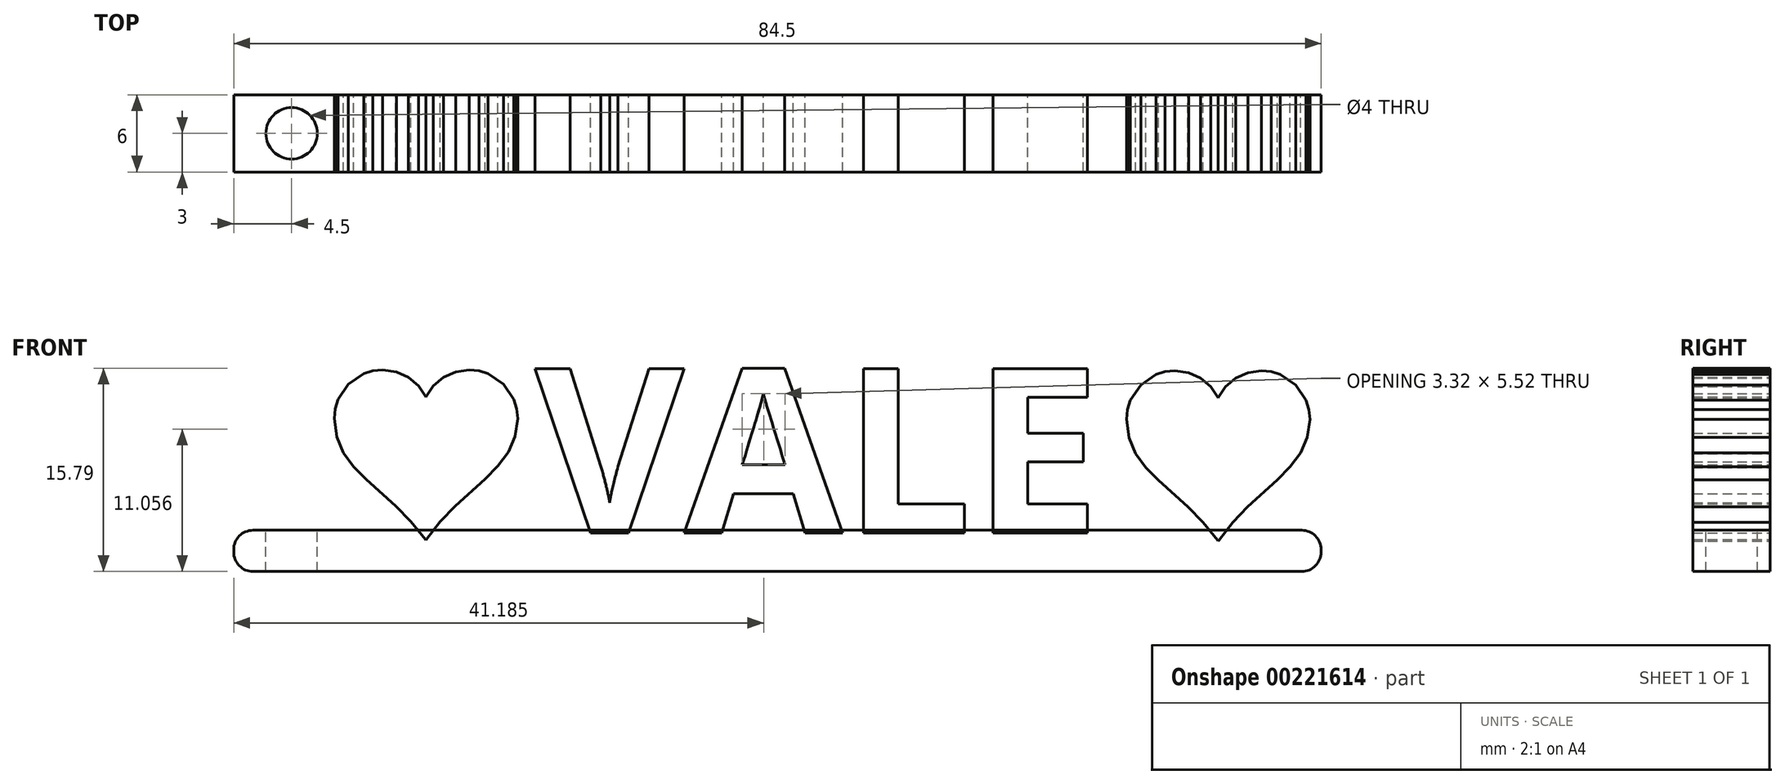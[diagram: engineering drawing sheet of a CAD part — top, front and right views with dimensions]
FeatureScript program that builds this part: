
annotation { "Feature Type Name" : "Feature", "Feature Type Description" : "" }
export const myFeature = defineFeature(function(context is Context, id is Id, definition is map)
    precondition{}
    {
        {
            var Q0;
            Q0=qCreatedBy(makeId("Front.planeOp"),FACE);
            var sketch = newSketch(context, id + "F0", { "sketchPlane" : qUnion([Q0])});
            skText(sketch, "E0", { "text": "   VALE", "fontName": "OpenSans-Bold.ttf"});
            skLineSegment(sketch, "E1", {"start": v(45.25, 12.6) * mm, "end": v(44.49, 12.52) * mm});
            skLineSegment(sketch, "E2", {"start": v(44.49, 12.52) * mm, "end": v(43.78, 12.3) * mm});
            skLineSegment(sketch, "E3", {"start": v(43.78, 12.3) * mm, "end": v(42.58, 11.5) * mm});
            skLineSegment(sketch, "E4", {"start": v(42.58, 11.5) * mm, "end": v(41.78, 10.3) * mm});
            skLineSegment(sketch, "E5", {"start": v(41.78, 10.3) * mm, "end": v(41.56, 9.59) * mm});
            skLineSegment(sketch, "E6", {"start": v(41.56, 9.59) * mm, "end": v(41.48, 8.83) * mm});
            skLineSegment(sketch, "E7", {"start": v(41.48, 8.83) * mm, "end": v(41.67, 7.39) * mm});
            skLineSegment(sketch, "E8", {"start": v(41.67, 7.39) * mm, "end": v(42.19, 6.16) * mm});
            skLineSegment(sketch, "E9", {"start": v(42.19, 6.16) * mm, "end": v(42.98, 5.08) * mm});
            skLineSegment(sketch, "E10", {"start": v(42.98, 5.08) * mm, "end": v(43.96, 4.08) * mm});
            skLineSegment(sketch, "E11", {"start": v(43.96, 4.08) * mm, "end": v(46.26, 2.03) * mm});
            skLineSegment(sketch, "E12", {"start": v(46.26, 2.03) * mm, "end": v(47.44, 0.82) * mm});
            skLineSegment(sketch, "E13", {"start": v(47.44, 0.82) * mm, "end": v(48.56, -0.59) * mm});
            skLineSegment(sketch, "E14", {"start": v(48.56, -0.59) * mm, "end": v(48.6, -0.65) * mm});
            skLineSegment(sketch, "E15", {"start": v(48.6, -0.65) * mm, "end": v(48.65, -0.59) * mm});
            skLineSegment(sketch, "E16", {"start": v(48.65, -0.59) * mm, "end": v(49.73, 0.82) * mm});
            skLineSegment(sketch, "E17", {"start": v(49.73, 0.82) * mm, "end": v(50.9, 2.03) * mm});
            skLineSegment(sketch, "E18", {"start": v(50.9, 2.03) * mm, "end": v(53.2, 4.12) * mm});
            skLineSegment(sketch, "E19", {"start": v(53.2, 4.12) * mm, "end": v(54.2, 5.13) * mm});
            skLineSegment(sketch, "E20", {"start": v(54.2, 5.13) * mm, "end": v(55, 6.21) * mm});
            skLineSegment(sketch, "E21", {"start": v(55, 6.21) * mm, "end": v(55.54, 7.42) * mm});
            skLineSegment(sketch, "E22", {"start": v(55.54, 7.42) * mm, "end": v(55.73, 8.83) * mm});
            skLineSegment(sketch, "E23", {"start": v(55.73, 8.83) * mm, "end": v(55.66, 9.59) * mm});
            skLineSegment(sketch, "E24", {"start": v(55.66, 9.59) * mm, "end": v(55.44, 10.3) * mm});
            skLineSegment(sketch, "E25", {"start": v(55.44, 10.3) * mm, "end": v(54.63, 11.5) * mm});
            skLineSegment(sketch, "E26", {"start": v(54.63, 11.5) * mm, "end": v(53.43, 12.3) * mm});
            skLineSegment(sketch, "E27", {"start": v(53.43, 12.3) * mm, "end": v(52.72, 12.52) * mm});
            skLineSegment(sketch, "E28", {"start": v(52.72, 12.52) * mm, "end": v(51.97, 12.6) * mm});
            skLineSegment(sketch, "E29", {"start": v(51.97, 12.6) * mm, "end": v(50.9, 12.44) * mm});
            skLineSegment(sketch, "E30", {"start": v(50.9, 12.44) * mm, "end": v(49.96, 12.01) * mm});
            skLineSegment(sketch, "E31", {"start": v(49.96, 12.01) * mm, "end": v(49.18, 11.35) * mm});
            skLineSegment(sketch, "E32", {"start": v(49.18, 11.35) * mm, "end": v(48.6, 10.5) * mm});
            skLineSegment(sketch, "E33", {"start": v(48.6, 10.5) * mm, "end": v(48.03, 11.35) * mm});
            skLineSegment(sketch, "E34", {"start": v(48.03, 11.35) * mm, "end": v(47.25, 12.01) * mm});
            skLineSegment(sketch, "E35", {"start": v(47.25, 12.01) * mm, "end": v(46.3, 12.44) * mm});
            skLineSegment(sketch, "E36", {"start": v(46.3, 12.44) * mm, "end": v(45.25, 12.6) * mm});
            skLineSegment(sketch, "E37", {"start": v(39.6, 12.85) * mm, "end": v(71.85, 12.85) * mm, "construction": true});
            skLineSegment(sketch, "E38", {"start": v(-16.32, 12.66) * mm, "end": v(-17.08, 12.59) * mm});
            skLineSegment(sketch, "E39", {"start": v(-17.08, 12.59) * mm, "end": v(-17.78, 12.37) * mm});
            skLineSegment(sketch, "E40", {"start": v(-17.78, 12.37) * mm, "end": v(-18.98, 11.56) * mm});
            skLineSegment(sketch, "E41", {"start": v(-18.98, 11.56) * mm, "end": v(-19.79, 10.36) * mm});
            skLineSegment(sketch, "E42", {"start": v(-19.79, 10.36) * mm, "end": v(-20, 9.65) * mm});
            skLineSegment(sketch, "E43", {"start": v(-20, 9.65) * mm, "end": v(-20.09, 8.9) * mm});
            skLineSegment(sketch, "E44", {"start": v(-20.09, 8.9) * mm, "end": v(-19.9, 7.45) * mm});
            skLineSegment(sketch, "E45", {"start": v(-19.9, 7.45) * mm, "end": v(-19.38, 6.22) * mm});
            skLineSegment(sketch, "E46", {"start": v(-19.38, 6.22) * mm, "end": v(-18.6, 5.15) * mm});
            skLineSegment(sketch, "E47", {"start": v(-18.6, 5.15) * mm, "end": v(-17.6, 4.15) * mm});
            skLineSegment(sketch, "E48", {"start": v(-17.6, 4.15) * mm, "end": v(-15.31, 2.09) * mm});
            skLineSegment(sketch, "E49", {"start": v(-15.31, 2.09) * mm, "end": v(-14.13, 0.89) * mm});
            skLineSegment(sketch, "E50", {"start": v(-14.13, 0.89) * mm, "end": v(-13, -0.52) * mm});
            skLineSegment(sketch, "E51", {"start": v(-13, -0.52) * mm, "end": v(-12.96, -0.59) * mm});
            skLineSegment(sketch, "E52", {"start": v(-12.96, -0.59) * mm, "end": v(-12.92, -0.52) * mm});
            skLineSegment(sketch, "E53", {"start": v(-12.92, -0.52) * mm, "end": v(-11.84, 0.89) * mm});
            skLineSegment(sketch, "E54", {"start": v(-11.84, 0.89) * mm, "end": v(-10.67, 2.1) * mm});
            skLineSegment(sketch, "E55", {"start": v(-10.67, 2.1) * mm, "end": v(-8.37, 4.19) * mm});
            skLineSegment(sketch, "E56", {"start": v(-8.37, 4.19) * mm, "end": v(-7.37, 5.2) * mm});
            skLineSegment(sketch, "E57", {"start": v(-7.37, 5.2) * mm, "end": v(-6.56, 6.28) * mm});
            skLineSegment(sketch, "E58", {"start": v(-6.56, 6.28) * mm, "end": v(-6.03, 7.49) * mm});
            skLineSegment(sketch, "E59", {"start": v(-6.03, 7.49) * mm, "end": v(-5.83, 8.9) * mm});
            skLineSegment(sketch, "E60", {"start": v(-5.83, 8.9) * mm, "end": v(-5.91, 9.65) * mm});
            skLineSegment(sketch, "E61", {"start": v(-5.91, 9.65) * mm, "end": v(-6.13, 10.36) * mm});
            skLineSegment(sketch, "E62", {"start": v(-6.13, 10.36) * mm, "end": v(-6.94, 11.56) * mm});
            skLineSegment(sketch, "E63", {"start": v(-6.94, 11.56) * mm, "end": v(-8.13, 12.37) * mm});
            skLineSegment(sketch, "E64", {"start": v(-8.13, 12.37) * mm, "end": v(-8.84, 12.59) * mm});
            skLineSegment(sketch, "E65", {"start": v(-8.84, 12.59) * mm, "end": v(-9.6, 12.66) * mm});
            skLineSegment(sketch, "E66", {"start": v(-9.6, 12.66) * mm, "end": v(-10.66, 12.5) * mm});
            skLineSegment(sketch, "E67", {"start": v(-10.66, 12.5) * mm, "end": v(-11.6, 12.08) * mm});
            skLineSegment(sketch, "E68", {"start": v(-11.6, 12.08) * mm, "end": v(-12.38, 11.41) * mm});
            skLineSegment(sketch, "E69", {"start": v(-12.38, 11.41) * mm, "end": v(-12.96, 10.56) * mm});
            skLineSegment(sketch, "E70", {"start": v(-12.96, 10.56) * mm, "end": v(-13.54, 11.41) * mm});
            skLineSegment(sketch, "E71", {"start": v(-13.54, 11.41) * mm, "end": v(-14.32, 12.08) * mm});
            skLineSegment(sketch, "E72", {"start": v(-14.32, 12.08) * mm, "end": v(-15.26, 12.5) * mm});
            skLineSegment(sketch, "E73", {"start": v(-15.26, 12.5) * mm, "end": v(-16.32, 12.66) * mm});
            const initialGuessF0  = {"E0": [-0.0184, 0, 1, 0, 0.01285]};
            skSetInitialGuess(sketch, initialGuessF0);
            skSolve(sketch);
        }
        {
            var Q0;
            Q0=qSketchRegion(id+"F0",true);
            extrude(context, id + "F1", {"entities" : qUnion([Q0]), "endBound" : BoundingType.SYMMETRIC, "depth" : 6 * mm});
        }
        {
            var Q0;
            Q0=qCreatedBy(makeId("Top.planeOp"),FACE);
            var sketch = newSketch(context, id + "F2", { "sketchPlane" : qUnion([Q0])});
            skLineSegment(sketch, "E74.bottom", {"start": v(-20.4, 3) * mm, "end": v(56.6, 3) * mm});
            skLineSegment(sketch, "E74.top", {"start": v(-20.4, -3) * mm, "end": v(56.6, -3) * mm});
            skLineSegment(sketch, "E74.left", {"start": v(-20.4, 3) * mm, "end": v(-20.4, -3) * mm});
            skLineSegment(sketch, "E74.right", {"start": v(56.6, 3) * mm, "end": v(56.6, -3) * mm});
            skSolve(sketch);
        }
        {
            var Q0;
            Q0=makeQuery(id+"F2.imprint","IMPRINT",FACE,{"disambiguationData":[TD([[makeQuery(id+"F2.imprint","IMPRINT",EDGE,{"derivedFrom":sQuery(id+"F2.wireOp",EDGE,"E74.bottom")}),-1.0]])]});
            extrude(context, id + "F3", {"entities" : qUnion([Q0]), "depth" : 0.2 * mm});
        }
        {
            var Q0;
            Q0=makeQuery(id+"F3.opExtrude","CAP_FACE",FACE,{"disambiguationData":[OSD([sQuery(id+"F2.wireOp",EDGE,"E74.bottom"),sQuery(id+"F2.wireOp",EDGE,"E74.top"),sQuery(id+"F2.wireOp",EDGE,"E74.left"),sQuery(id+"F2.wireOp",EDGE,"E74.right")])],"isStart":true});
            extrude(context, id + "F4", {"entities" : qUnion([Q0]), "depth" : 3 * mm});
        }
        {
            var Q0;
            {var subQ0=sQuery(id+"F2.wireOp",EDGE,"E74.left");Q0=makeQuery(id+"FaVoHrOpcFZXiYX_6.opBoolean","MERGE",FACE,{"derivedFrom":[makeQuery(id+"F3.opExtrude","SWEPT_FACE",FACE,{"disambiguationData":[OSD([subQ0])]}),makeQuery(id+"F4.opExtrude","SWEPT_FACE",FACE,{"disambiguationData":[OSD([subQ0])]})]});}
            var sketch = newSketch(context, id + "F5", { "sketchPlane" : qUnion([Q0])});
            skLineSegment(sketch, "E75.bottom", {"start": v(-3, -3) * mm, "end": v(3, -3) * mm});
            skLineSegment(sketch, "E75.top", {"start": v(-3, 0.2) * mm, "end": v(3, 0.2) * mm});
            skLineSegment(sketch, "E75.left", {"start": v(-3, -3) * mm, "end": v(-3, 0.2) * mm});
            skLineSegment(sketch, "E75.right", {"start": v(3, -3) * mm, "end": v(3, 0.2) * mm});
            skSolve(sketch);
        }
        {
            var Q0;
            Q0=qSketchRegion(id+"F5",true);
            extrude(context, id + "F6", {"entities" : qUnion([Q0]), "operationType" : NewBodyOperationType.ADD, "depth" : 7.5 * mm});
        }
        {
            var Q0;
            Q0=makeQuery(id+"F6.opExtrude","CAP_EDGE",EDGE,{"disambiguationData":[OSD([sQuery(id+"F5.wireOp",EDGE,"E75.bottom")])],"isStart":false});
            var Q1;
            Q1=makeQuery(id+"F6.opExtrude","CAP_EDGE",EDGE,{"disambiguationData":[OSD([sQuery(id+"F5.wireOp",EDGE,"E75.top")])],"isStart":false});
            var Q2;
            Q2=makeQuery(id+"F4.opExtrude","CAP_EDGE",EDGE,{"disambiguationData":[OSD([sQuery(id+"F2.wireOp",EDGE,"E74.right")])],"isStart":false});
            fillet(context, id + "F7", {"entities" : qUnion([Q0, Q1, Q2]), "radius" : 1.5 * mm, "tangentPropagation" : true, "allowEdgeOverflow" : false});
        }
        {
            var Q0;
            {var subQ19=sQuery(id+"F2.wireOp",EDGE,"E74.top");var subQ20=sQuery(id+"F2.wireOp",EDGE,"E74.bottom");var subQ63=sQuery(id+"F0.wireOp",EDGE,"E0.sketch_text.stroke-2");var subQ66=sQuery(id+"F2.wireOp",EDGE,"E74.left");Q0=makeQuery(id+"F6.boolean.opBoolean","MERGE",FACE,{"derivedFrom":[makeQuery(id+"FaVoHrOpcFZXiYX_6.opBoolean","SPLIT",FACE,{"disambiguationData":[TD([makeQuery(id+"F1.opExtrude","SWEPT_FACE",FACE,{"disambiguationData":[OSD([subQ63])]})])],"derivedFrom":makeQuery(id+"F3.opExtrude","CAP_FACE",FACE,{"disambiguationData":[OSD([subQ20,subQ19,subQ66,sQuery(id+"F2.wireOp",EDGE,"E74.right")])],"isStart":false})}),makeQuery(id+"F6.opExtrude","SWEPT_FACE",FACE,{"disambiguationData":[OSD([sQuery(id+"F5.wireOp",EDGE,"E75.top")])]})]});}
            var sketch = newSketch(context, id + "F8", { "sketchPlane" : qUnion([Q0])});
            skCircle(sketch, "E76", {"center": v(-23.4, 0) * mm, "radius": 2 * mm});
            skSolve(sketch);
        }
        {
            var Q0;
            Q0=makeQuery(id+"F8.imprint","IMPRINT",FACE,{"disambiguationData":[TD([[makeQuery(id+"F8.imprint","IMPRINT",EDGE,{"derivedFrom":sQuery(id+"F8.wireOp",EDGE,"E76")}),1.0]])]});
            extrude(context, id + "F9", {"entities" : qUnion([Q0]), "operationType" : NewBodyOperationType.REMOVE, "oppositeDirection" : true, "depth" : 4 * mm});
        }
        {
            var Q0;
            Q0=makeQuery(id+"F3.opExtrude","CAP_EDGE",EDGE,{"disambiguationData":[OSD([sQuery(id+"F2.wireOp",EDGE,"E74.right")])],"isStart":false});
            fillet(context, id + "F10", {"entities" : qUnion([Q0]), "radius" : 1.5 * mm, "tangentPropagation" : true, "allowEdgeOverflow" : false});
        }
    });
